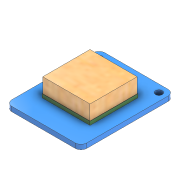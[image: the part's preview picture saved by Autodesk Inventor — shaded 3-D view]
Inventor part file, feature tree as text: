
AUTODESK INVENTOR PART (.ipt)
format: ipt  version: 2022.3 (Build 263350000, 350)  size: 141,312 bytes
history: native  units: mm
features: extrude x3, sketch x3, other x1
ambient origin geometry x8: Origin, YZ Plane, XZ Plane, XY Plane, X Axis, Y Axis, Z Axis, Center Point
bodies: Body1 (feature_tree)
feature tree (7):
  other  "Sólido1"
  extrude  "Extrusión1"  Depth=31.5mm
  extrude  "Extrusión2"  Depth=2.0mm
  extrude  "Extrusión3"  Depth=1.2mm
  sketch  "Boceto1"  dims[d0=25.4mm d1=31.5mm]
  sketch  "Boceto2"  dims[d2=2.0mm d3=2.54mm]
  sketch  "Boceto3"  dims[d4=10.16mm d5=10.16mm d6=2.3mm d7=2.3mm d8=1.6mm d9=0.0mm d10=16.0mm d11=16.0mm d12=6.2mm d13=0.0mm d14=16.2mm d15=16.2mm d16=1.2mm d17=0.0mm]
